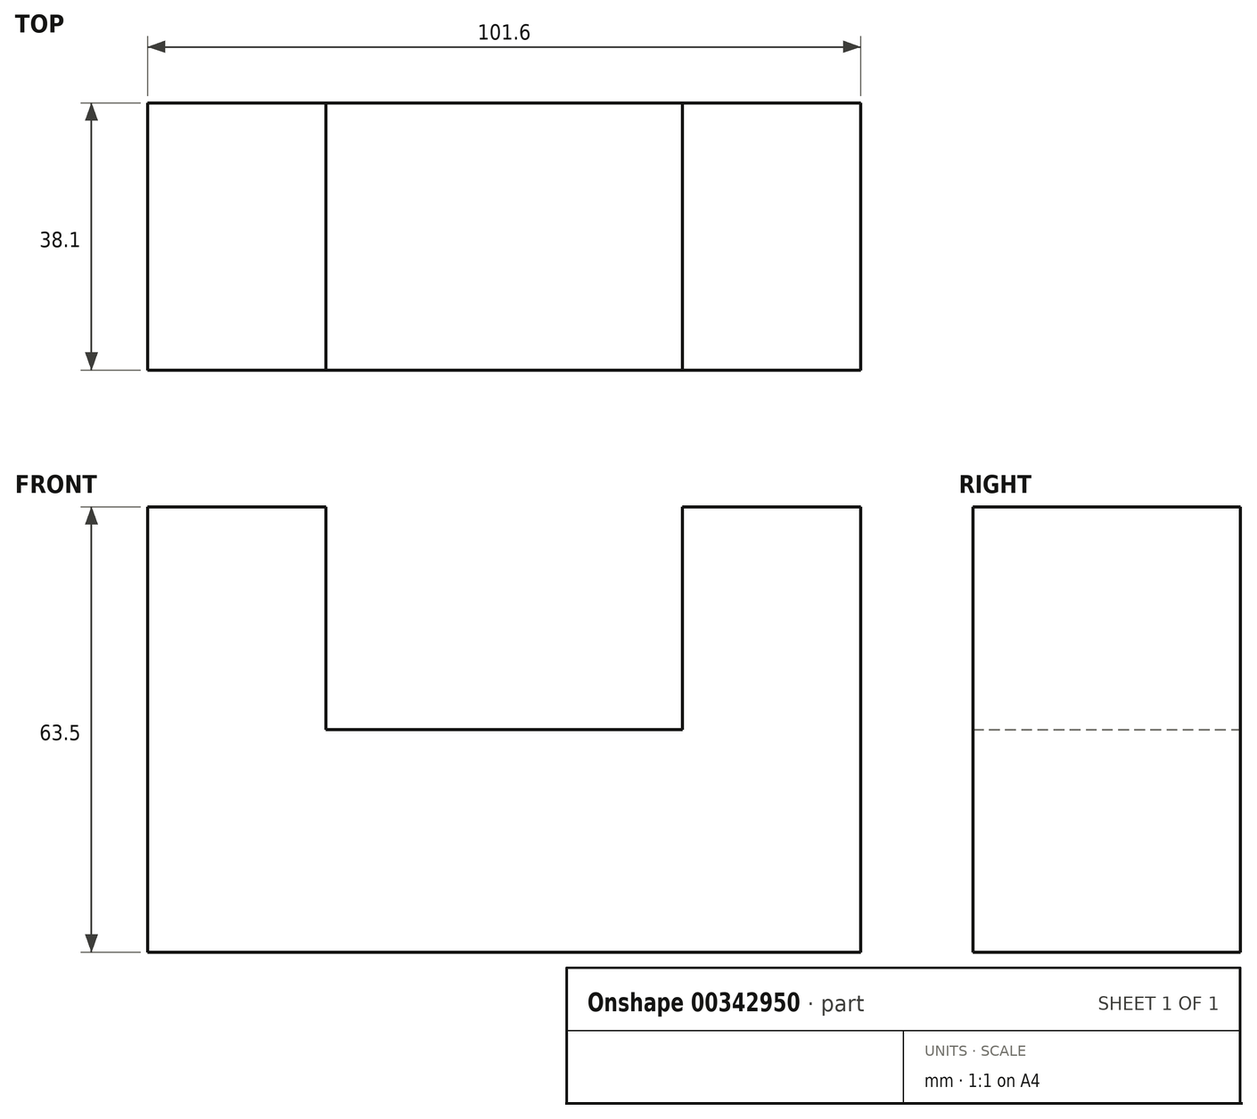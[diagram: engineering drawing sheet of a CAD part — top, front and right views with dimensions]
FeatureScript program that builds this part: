
annotation { "Feature Type Name" : "Feature", "Feature Type Description" : "" }
export const myFeature = defineFeature(function(context is Context, id is Id, definition is map)
    precondition{}
    {
        {
            var Q0;
            Q0=qCreatedBy(makeId("Front.planeOp"),FACE);
            var sketch = newSketch(context, id + "F0", { "sketchPlane" : qUnion([Q0])});
            skLineSegment(sketch, "E0", {"start": v(52.57, 45.5) * mm, "end": v(52.57, -18) * mm});
            skLineSegment(sketch, "E1", {"start": v(52.57, -18) * mm, "end": v(-49.03, -18) * mm});
            skLineSegment(sketch, "E2", {"start": v(-49.03, -18) * mm, "end": v(-49.03, 45.5) * mm});
            skLineSegment(sketch, "E3", {"start": v(-49.03, 45.5) * mm, "end": v(-23.63, 45.5) * mm});
            skLineSegment(sketch, "E4", {"start": v(52.57, 45.5) * mm, "end": v(27.17, 45.5) * mm});
            skLineSegment(sketch, "E5", {"start": v(27.17, 45.5) * mm, "end": v(27.17, 13.76) * mm});
            skLineSegment(sketch, "E6", {"start": v(-23.63, 45.5) * mm, "end": v(-23.63, 13.76) * mm});
            skLineSegment(sketch, "E7", {"start": v(-23.63, 13.76) * mm, "end": v(27.17, 13.76) * mm});
            skSolve(sketch);
        }
        {
            var Q0;
            Q0 = qSketchRegion(id + "F0", true);
            extrude(context, id + "F1", {"entities" : qUnion([Q0]), "depth" : 38.1 * mm});
        }
    });
